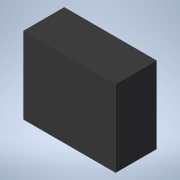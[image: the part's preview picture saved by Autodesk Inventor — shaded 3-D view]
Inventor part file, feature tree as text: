
AUTODESK INVENTOR PART (.ipt)
format: ipt  version: 2021 (Build 250183000, 183)  size: 102,912 bytes
history: native  units: mm
features: reference x5, other x3, extrude x2, sketch x2, chamfer x1
ambient origin geometry x8: Origin, YZ Plane, XZ Plane, XY Plane, X Axis, Y Axis, Z Axis, Center Point
bodies: Volumenkörper1 (feature_tree)
feature tree (13):
  extrude  "Extrusion1"  Depth=6.4mm TaperAngle=0.0deg
  extrude  "Extrusion2"  Depth=5.4mm TaperAngle=45.0deg
  chamfer  "Fase1"  [1 undecoded]
  sketch  "Skizze1"  dims[d0=3.35mm d1=6.4mm d2=0.0mm]
  reference  "Referenz1"
  reference  "Referenz2"
  reference  "Referenz3"
  reference  "Referenz4"
  reference  "Referenz5"
  sketch  "Skizze2"  dims[d3=5.4mm d4=0.0mm d5=0.6mm d6=2.0mm d7=45.0deg]
  other  "<userpath>\Desktop\Bachelorarbeit\CAD\00_RobotAssembly.iam"
  other  "00_RobotAssembly.iam"
  other  "12_Motor_Fixation:1"
note: 1 required parameter value undecoded (feature->parameter linkage not recoverable at this tier; creation-order binding heuristic only, values carry confidence <= 0.55)
